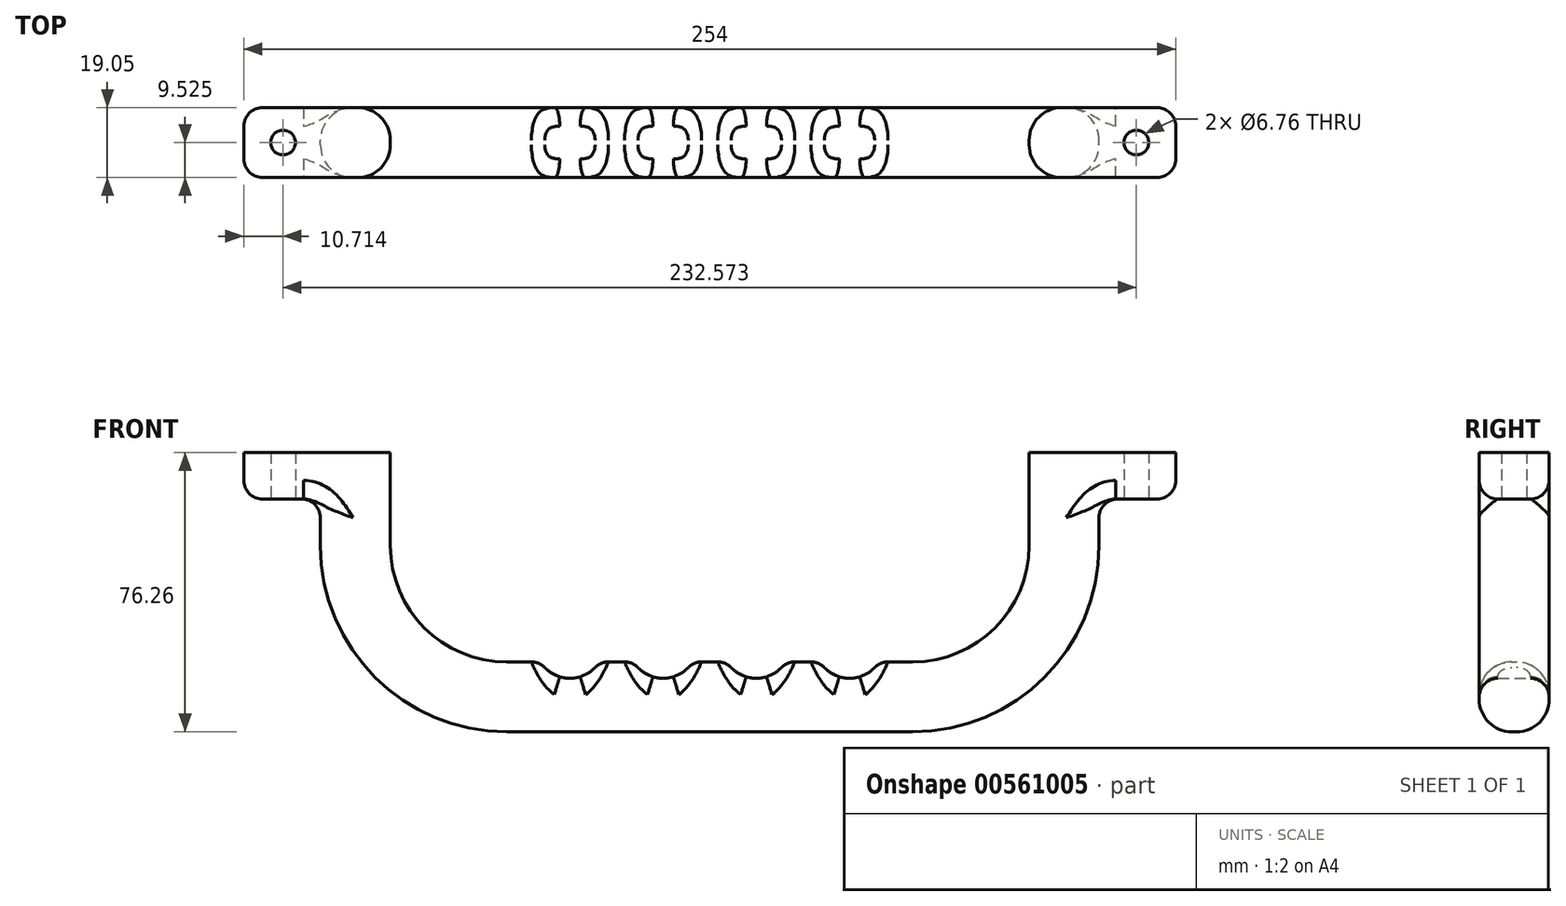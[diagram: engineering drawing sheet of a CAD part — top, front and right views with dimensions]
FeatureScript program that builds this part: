
annotation { "Feature Type Name" : "Feature", "Feature Type Description" : "" }
export const myFeature = defineFeature(function(context is Context, id is Id, definition is map)
    precondition{}
    {
        {
            var Q0;
            Q0=qCreatedBy(makeId("Front.planeOp"),FACE);
            var sketch = newSketch(context, id + "F0", { "sketchPlane" : qUnion([Q0])});
            skLineSegment(sketch, "E0.top", {"start": v(-55.3, -76.2) * mm, "end": v(55.3, -76.2) * mm});
            skLineSegment(sketch, "E0.left", {"start": v(-127, 0) * mm, "end": v(-127, -12.7) * mm});
            skLineSegment(sketch, "E0.right", {"start": v(127, 0.06) * mm, "end": v(127, -12.7) * mm});
            skLineSegment(sketch, "E1", {"start": v(127, -12.7) * mm, "end": v(106.1, -12.7) * mm});
            skLineSegment(sketch, "E2", {"start": v(106.1, -12.7) * mm, "end": v(106.1, -25.4) * mm});
            skLineSegment(sketch, "E3", {"start": v(-127, -12.7) * mm, "end": v(-106.1, -12.7) * mm});
            skLineSegment(sketch, "E4", {"start": v(-106.1, -12.7) * mm, "end": v(-106.1, -25.4) * mm});
            skPoint(sketch, "E5.visualSharp", {"position": v(-106.1, -76.2) * mm});
            skArc(sketch, "E5.filletArc", {"start": v(-106.1, -25.4) * mm, "mid": v(-91.22, -61.32) * mm, "end": v(-55.3, -76.2) * mm});
            skPoint(sketch, "E6.visualSharp", {"position": v(106.1, -76.2) * mm});
            skArc(sketch, "E6.filletArc", {"start": v(55.3, -76.2) * mm, "mid": v(91.22, -61.32) * mm, "end": v(106.1, -25.4) * mm});
            skLineSegment(sketch, "E7.0", {"start": v(87.05, -12.7) * mm, "end": v(87.05, -25.4) * mm});
            skLineSegment(sketch, "E7.1", {"start": v(-87.05, -12.7) * mm, "end": v(-87.05, -25.4) * mm});
            skArc(sketch, "E7.2", {"start": v(-87.05, -25.4) * mm, "mid": v(-77.75, -47.85) * mm, "end": v(-55.3, -57.15) * mm});
            skLineSegment(sketch, "E7.3", {"start": v(-55.3, -57.15) * mm, "end": v(55.3, -57.15) * mm});
            skArc(sketch, "E7.4", {"start": v(55.3, -57.15) * mm, "mid": v(77.75, -47.85) * mm, "end": v(87.05, -25.4) * mm});
            skLineSegment(sketch, "E8", {"start": v(-127, 0) * mm, "end": v(-87.05, 0) * mm});
            skLineSegment(sketch, "E9", {"start": v(-87.05, 0) * mm, "end": v(-87.05, -12.7) * mm});
            skLineSegment(sketch, "E10", {"start": v(127, 0.06) * mm, "end": v(87.05, 0.06) * mm});
            skLineSegment(sketch, "E11", {"start": v(87.05, 0.06) * mm, "end": v(87.05, -12.7) * mm});
            skSolve(sketch);
        }
        {
            var Q0;
            Q0=makeQuery(id+"F0.imprint","IMPRINT",FACE,{"disambiguationData":[TD([[makeQuery(id+"F0.imprint","IMPRINT",EDGE,{"derivedFrom":sQuery(id+"F0.wireOp",EDGE,"E0.top")}),1.0]])]});
            extrude(context, id + "F1", {"entities" : qUnion([Q0]), "depth" : 19.05 * mm, "offsetDistance" : 25.4 * mm});
        }
        {
            var Q0;
            Q0=makeQuery(id+"F1.opExtrude","CAP_EDGE",EDGE,{"disambiguationData":[OSD([sQuery(id+"F0.wireOp",EDGE,"E5.filletArc")])],"isStart":false});
            var Q1;
            Q1=makeQuery(id+"F1.opExtrude","SWEPT_FACE",FACE,{"disambiguationData":[OSD([sQuery(id+"F0.wireOp",EDGE,"E0.top")])]});
            var Q2;
            Q2=makeQuery(id+"F1.opExtrude","CAP_EDGE",EDGE,{"disambiguationData":[OSD([sQuery(id+"F0.wireOp",EDGE,"E7.3")])],"isStart":true});
            var Q3;
            Q3=makeQuery(id+"F1.opExtrude","CAP_EDGE",EDGE,{"disambiguationData":[OSD([sQuery(id+"F0.wireOp",EDGE,"E7.3")])],"isStart":false});
            fillet(context, id + "F2", {"entities" : qUnion([Q0, Q1, Q2, Q3]), "radius" : 8.9 * mm, "tangentPropagation" : true, "allowEdgeOverflow" : false});
        }
        {
            var Q0;
            Q0=makeQuery(id+"F1.opExtrude","CAP_EDGE",EDGE,{"disambiguationData":[OSD([sQuery(id+"F0.wireOp",EDGE,"E0.right")])],"isStart":false});
            var Q1;
            Q1=makeQuery(id+"F1.opExtrude","CAP_EDGE",EDGE,{"disambiguationData":[OSD([sQuery(id+"F0.wireOp",EDGE,"E0.right")])],"isStart":true});
            var Q2;
            Q2=makeQuery(id+"F1.opExtrude","SWEPT_FACE",FACE,{"disambiguationData":[OSD([sQuery(id+"F0.wireOp",EDGE,"E1")])]});
            var Q3;
            Q3=makeQuery(id+"F1.opExtrude","SWEPT_FACE",FACE,{"disambiguationData":[OSD([sQuery(id+"F0.wireOp",EDGE,"E3")])]});
            var Q4;
            Q4=makeQuery(id+"F1.opExtrude","CAP_EDGE",EDGE,{"disambiguationData":[OSD([sQuery(id+"F0.wireOp",EDGE,"E0.left")])],"isStart":true});
            var Q5;
            Q5=makeQuery(id+"F1.opExtrude","CAP_EDGE",EDGE,{"disambiguationData":[OSD([sQuery(id+"F0.wireOp",EDGE,"E0.left")])],"isStart":false});
            fillet(context, id + "F3", {"entities" : qUnion([Q0, Q1, Q2, Q3, Q4, Q5]), "radius" : 5.08 * mm, "tangentPropagation" : true, "allowEdgeOverflow" : false});
        }
        {
            var Q0;
            Q0=makeQuery(id+"F1.opExtrude","SWEPT_FACE",FACE,{"disambiguationData":[OSD([sQuery(id+"F0.wireOp",EDGE,"E3")])]});
            var sketch = newSketch(context, id + "F4", { "sketchPlane" : qUnion([Q0])});
            skPoint(sketch, "E12", {"position": v(-116.29, 9.53) * mm});
            skLineSegment(sketch, "E13", {"start": v(-121.92, 13.97) * mm, "end": v(-110.65, 5.08) * mm, "construction": true});
            skLineSegment(sketch, "E14", {"start": v(0, 0) * mm, "end": v(0, 19.05) * mm, "construction": true});
            skPoint(sketch, "E15.MirrorP", {"position": v(116.29, 9.53) * mm});
            skSolve(sketch);
        }
        {
            var Q0;
            Q0=sQuery(id+"F4.wireOp",VERTEX,"E12");
            var Q1;
            Q1=sQuery(id+"F4.wireOp",VERTEX,"E15.MirrorP");
            var Q2;
            Q2=makeQuery(id+"F1.opExtrude","SWEPT_BODY",BODY,{"disambiguationData":[OSD([sQuery(id+"F0.wireOp",EDGE,"E0.top"),sQuery(id+"F0.wireOp",EDGE,"E0.left"),sQuery(id+"F0.wireOp",EDGE,"E0.right"),sQuery(id+"F0.wireOp",EDGE,"E1"),sQuery(id+"F0.wireOp",EDGE,"E2"),sQuery(id+"F0.wireOp",EDGE,"E3"),sQuery(id+"F0.wireOp",EDGE,"E4"),sQuery(id+"F0.wireOp",EDGE,"E5.filletArc"),sQuery(id+"F0.wireOp",EDGE,"E6.filletArc"),sQuery(id+"F0.wireOp",EDGE,"E7.0"),sQuery(id+"F0.wireOp",EDGE,"E7.1"),sQuery(id+"F0.wireOp",EDGE,"E7.2"),sQuery(id+"F0.wireOp",EDGE,"E7.3"),sQuery(id+"F0.wireOp",EDGE,"E7.4"),sQuery(id+"F0.wireOp",EDGE,"E8"),sQuery(id+"F0.wireOp",EDGE,"E9"),sQuery(id+"F0.wireOp",EDGE,"E10"),sQuery(id+"F0.wireOp",EDGE,"E11")])]});
            hole(context, id + "F5", {"style" : HoleStyle.SIMPLE, "endStyle" : HoleEndStyle.BLIND, "standardTappedOrClearance" : lookupTablePath({ "standard" : "ANSI", "fit" : "Normal (ASME)", "size" : "1/4", "type" : "Clearance" }), "standardBlindInLast" : lookupTablePath({ "fit" : "Free", "standard" : "ANSI", "size" : "1/4", "type" : "Clearance" }), "holeDiameter" : 6.76 * mm, "holeDepth" : 152.4 * mm, "isTappedThrough" : true, "tappedDepth" : 12.7 * mm, "tapClearance" : 3, "locations" : qUnion([Q0, Q1]), "scope" : qUnion([Q2])});
        }
        {
            var Q0;
            Q0=qCreatedBy(makeId("Front.planeOp"),FACE);
            var sketch = newSketch(context, id + "F6", { "sketchPlane" : qUnion([Q0])});
            skCircle(sketch, "E16", {"center": v(38.1, -52.07) * mm, "radius": 9.53 * mm});
            skCircle(sketch, "E17.1.0.0", {"center": v(12.7, -52.07) * mm, "radius": 9.53 * mm});
            skCircle(sketch, "E17.2.0.0", {"center": v(-12.7, -52.07) * mm, "radius": 9.53 * mm});
            skCircle(sketch, "E17.3.0.0", {"center": v(-38.1, -52.07) * mm, "radius": 9.53 * mm});
            skLineSegment(sketch, "E17.direction1", {"start": v(38.1, -52.07) * mm, "end": v(12.7, -52.07) * mm, "construction": true});
            skLineSegment(sketch, "E18", {"start": v(-12.7, -52.07) * mm, "end": v(0, -52.07) * mm});
            skLineSegment(sketch, "E19", {"start": v(0, -52.07) * mm, "end": v(12.7, -52.07) * mm});
            skLineSegment(sketch, "E20", {"start": v(0, -52.07) * mm, "end": v(0, -67.31) * mm, "construction": true});
            skSolve(sketch);
        }
        {
            var Q0;
            Q0=makeQuery(id+"F6.imprint","IMPRINT",FACE,{"disambiguationData":[TD([[makeQuery(id+"F6.imprint","IMPRINT",EDGE,{"derivedFrom":sQuery(id+"F6.wireOp",EDGE,"E16")}),1.0]])]});
            var Q1;
            Q1=makeQuery(id+"F6.imprint","IMPRINT",FACE,{"disambiguationData":[TD([[makeQuery(id+"F6.imprint","IMPRINT",EDGE,{"derivedFrom":sQuery(id+"F6.wireOp",EDGE,"E17.1.0.0")}),1.0]])]});
            var Q2;
            Q2=makeQuery(id+"F6.imprint","IMPRINT",FACE,{"disambiguationData":[TD([[makeQuery(id+"F6.imprint","IMPRINT",EDGE,{"derivedFrom":sQuery(id+"F6.wireOp",EDGE,"E17.2.0.0")}),1.0]])]});
            var Q3;
            Q3=makeQuery(id+"F6.imprint","IMPRINT",FACE,{"disambiguationData":[TD([[makeQuery(id+"F6.imprint","IMPRINT",EDGE,{"derivedFrom":sQuery(id+"F6.wireOp",EDGE,"E17.3.0.0")}),1.0]])]});
            extrude(context, id + "F7", {"entities" : qUnion([Q0, Q1, Q2, Q3]), "operationType" : NewBodyOperationType.REMOVE, "depth" : 25.4 * mm, "offsetDistance" : 25.4 * mm});
        }
        {
            var Q0;
            Q0=makeQuery(id+"F7.boolean.opBoolean","COPY",FACE,{"derivedFrom":makeQuery(id+"F7.opExtrude","SWEPT_FACE",FACE,{"disambiguationData":[OSD([sQuery(id+"F6.wireOp",EDGE,"E16")])]})});
            var Q1;
            Q1=makeQuery(id+"F7.boolean.opBoolean","COPY",FACE,{"derivedFrom":makeQuery(id+"F7.opExtrude","SWEPT_FACE",FACE,{"disambiguationData":[OSD([sQuery(id+"F6.wireOp",EDGE,"E17.1.0.0")])]})});
            var Q2;
            Q2=makeQuery(id+"F7.boolean.opBoolean","COPY",FACE,{"derivedFrom":makeQuery(id+"F7.opExtrude","SWEPT_FACE",FACE,{"disambiguationData":[OSD([sQuery(id+"F6.wireOp",EDGE,"E17.2.0.0")])]})});
            var Q3;
            Q3=makeQuery(id+"F7.boolean.opBoolean","COPY",FACE,{"derivedFrom":makeQuery(id+"F7.opExtrude","SWEPT_FACE",FACE,{"disambiguationData":[OSD([sQuery(id+"F6.wireOp",EDGE,"E17.3.0.0")])]})});
            fillet(context, id + "F8", {"entities" : qUnion([Q0, Q1, Q2, Q3]), "radius" : 5.08 * mm, "tangentPropagation" : true, "allowEdgeOverflow" : false});
        }
    });
